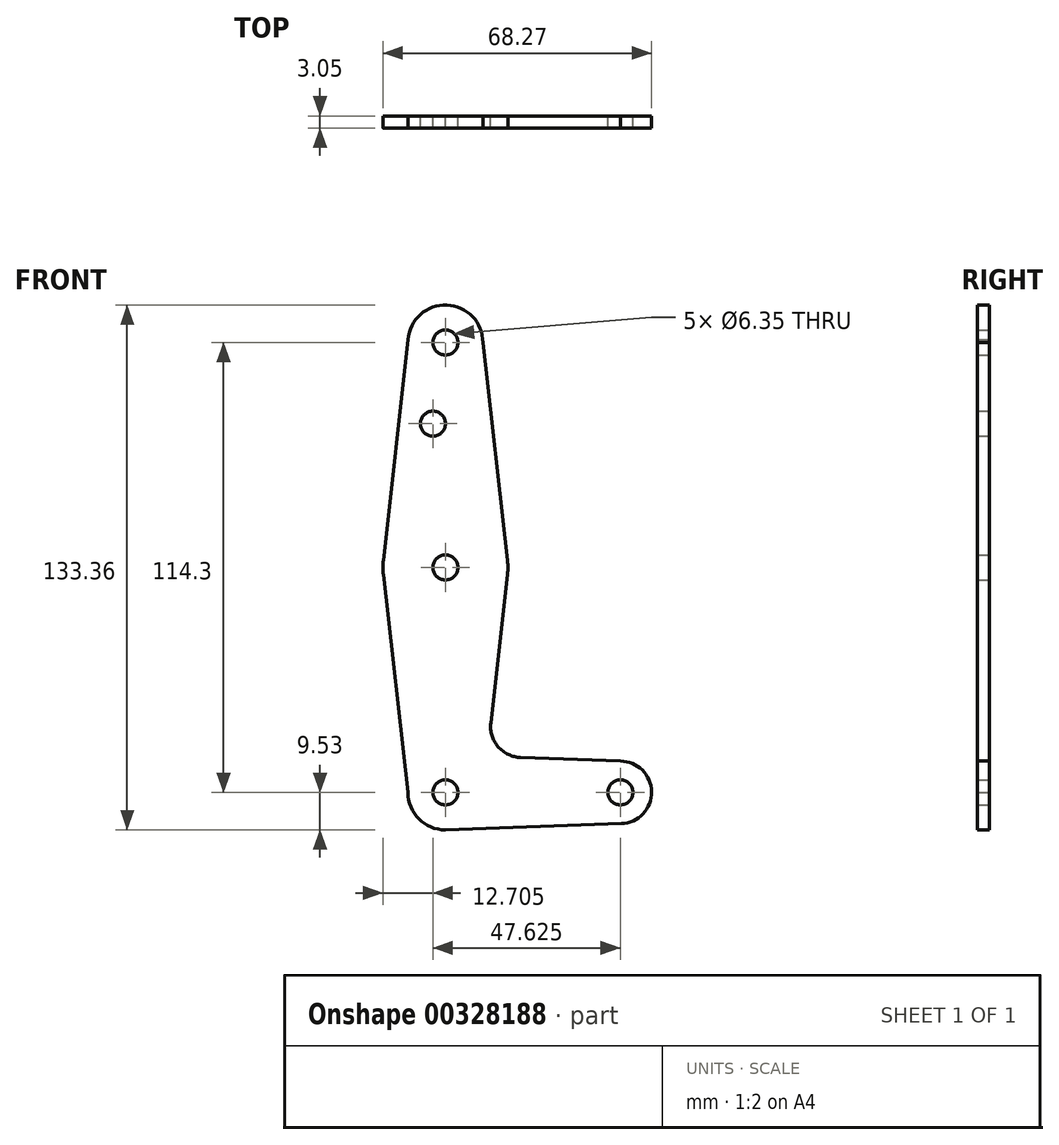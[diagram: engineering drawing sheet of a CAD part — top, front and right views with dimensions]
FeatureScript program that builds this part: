
annotation { "Feature Type Name" : "Feature", "Feature Type Description" : "" }
export const myFeature = defineFeature(function(context is Context, id is Id, definition is map)
    precondition{}
    {
        {
            var Q0;
            Q0=qCreatedBy(makeId("Front.planeOp"),FACE);
            var sketch = newSketch(context, id + "F0", { "sketchPlane" : qUnion([Q0])});
            skLineSegment(sketch, "E0", {"start": v(0, 0) * mm, "end": v(0, 114.3) * mm, "construction": true});
            skLineSegment(sketch, "E1", {"start": v(0, 0) * mm, "end": v(44.45, 0) * mm, "construction": true});
            skCircle(sketch, "E2", {"center": v(44.45, 0) * mm, "radius": 7.94 * mm});
            skCircle(sketch, "E3", {"center": v(0, 0) * mm, "radius": 9.53 * mm});
            skCircle(sketch, "E4", {"center": v(0, 114.3) * mm, "radius": 9.53 * mm});
            skCircle(sketch, "E5", {"center": v(0, 57.15) * mm, "radius": 15.88 * mm});
            skLineSegment(sketch, "E6", {"start": v(9.52, 114.28) * mm, "end": v(15.77, 58.93) * mm});
            skLineSegment(sketch, "E7", {"start": v(-9.5, 115.05) * mm, "end": v(-15.77, 58.93) * mm});
            skLineSegment(sketch, "E8", {"start": v(11.52, 17.68) * mm, "end": v(15.77, 55.37) * mm});
            skLineSegment(sketch, "E9", {"start": v(-9.53, 0) * mm, "end": v(-15.77, 55.37) * mm});
            skPoint(sketch, "E10.startSnap0", {"position": v(12.13, 23.07) * mm});
            skCircle(sketch, "E11", {"center": v(0, 114.3) * mm, "radius": 3.18 * mm});
            skCircle(sketch, "E12", {"center": v(-3.18, 93.68) * mm, "radius": 3.18 * mm});
            skCircle(sketch, "E13", {"center": v(0, 0) * mm, "radius": 3.18 * mm});
            skCircle(sketch, "E14", {"center": v(44.45, 0) * mm, "radius": 3.18 * mm});
            skCircle(sketch, "E15", {"center": v(0, 57.15) * mm, "radius": 3.18 * mm});
            skLineSegment(sketch, "E16", {"start": v(44.45, 7.94) * mm, "end": v(19.14, 8.85) * mm});
            skPoint(sketch, "E17.newPointB", {"position": v(0, 9.53) * mm});
            skArc(sketch, "E17.filletArc", {"start": v(11.52, 17.68) * mm, "mid": v(13.4, 11.6) * mm, "end": v(19.14, 8.85) * mm});
            skLineSegment(sketch, "E18", {"start": v(0, -9.53) * mm, "end": v(44.73, -7.93) * mm});
            skSolve(sketch);
        }
        {
            var Q0;
            Q0=makeQuery(id+"F0.imprint","IMPRINT",FACE,{"disambiguationData":[TD([[makeQuery(id+"F0.imprint","IMPRINT",EDGE,{"derivedFrom":sQuery(id+"F0.wireOp",EDGE,"E11")}),-1.0]])]});
            var Q1;
            {var subQ0=sQuery(id+"F0.wireOp",EDGE,"E6");Q1=makeQuery(id+"F0.imprint","IMPRINT",FACE,{"disambiguationData":[TD([[makeQuery(id+"F0.imprint","IMPRINT",EDGE,{"derivedFrom":subQ0}),-1.0]])]});}
            var Q2;
            Q2=makeQuery(id+"F0.imprint","IMPRINT",FACE,{"disambiguationData":[TD([[makeQuery(id+"F0.imprint","IMPRINT",EDGE,{"derivedFrom":sQuery(id+"F0.wireOp",EDGE,"E15")}),-1.0]])]});
            var Q3;
            {var subQ0=sQuery(id+"F0.wireOp",EDGE,"E8");Q3=makeQuery(id+"F0.imprint","IMPRINT",FACE,{"disambiguationData":[TD([[makeQuery(id+"F0.imprint","IMPRINT",EDGE,{"derivedFrom":subQ0}),1.0]])]});}
            var Q4;
            Q4=makeQuery(id+"F0.imprint","IMPRINT",FACE,{"disambiguationData":[TD([[makeQuery(id+"F0.imprint","IMPRINT",EDGE,{"derivedFrom":sQuery(id+"F0.wireOp",EDGE,"E13")}),-1.0]])]});
            var Q5;
            Q5=makeQuery(id+"F0.imprint","IMPRINT",FACE,{"disambiguationData":[TD([[makeQuery(id+"F0.imprint","IMPRINT",EDGE,{"derivedFrom":sQuery(id+"F0.wireOp",EDGE,"E14")}),-1.0]])]});
            extrude(context, id + "F1", {"entities" : qUnion([Q0, Q1, Q2, Q3, Q4, Q5]), "depth" : 3.05 * mm});
        }
    });
